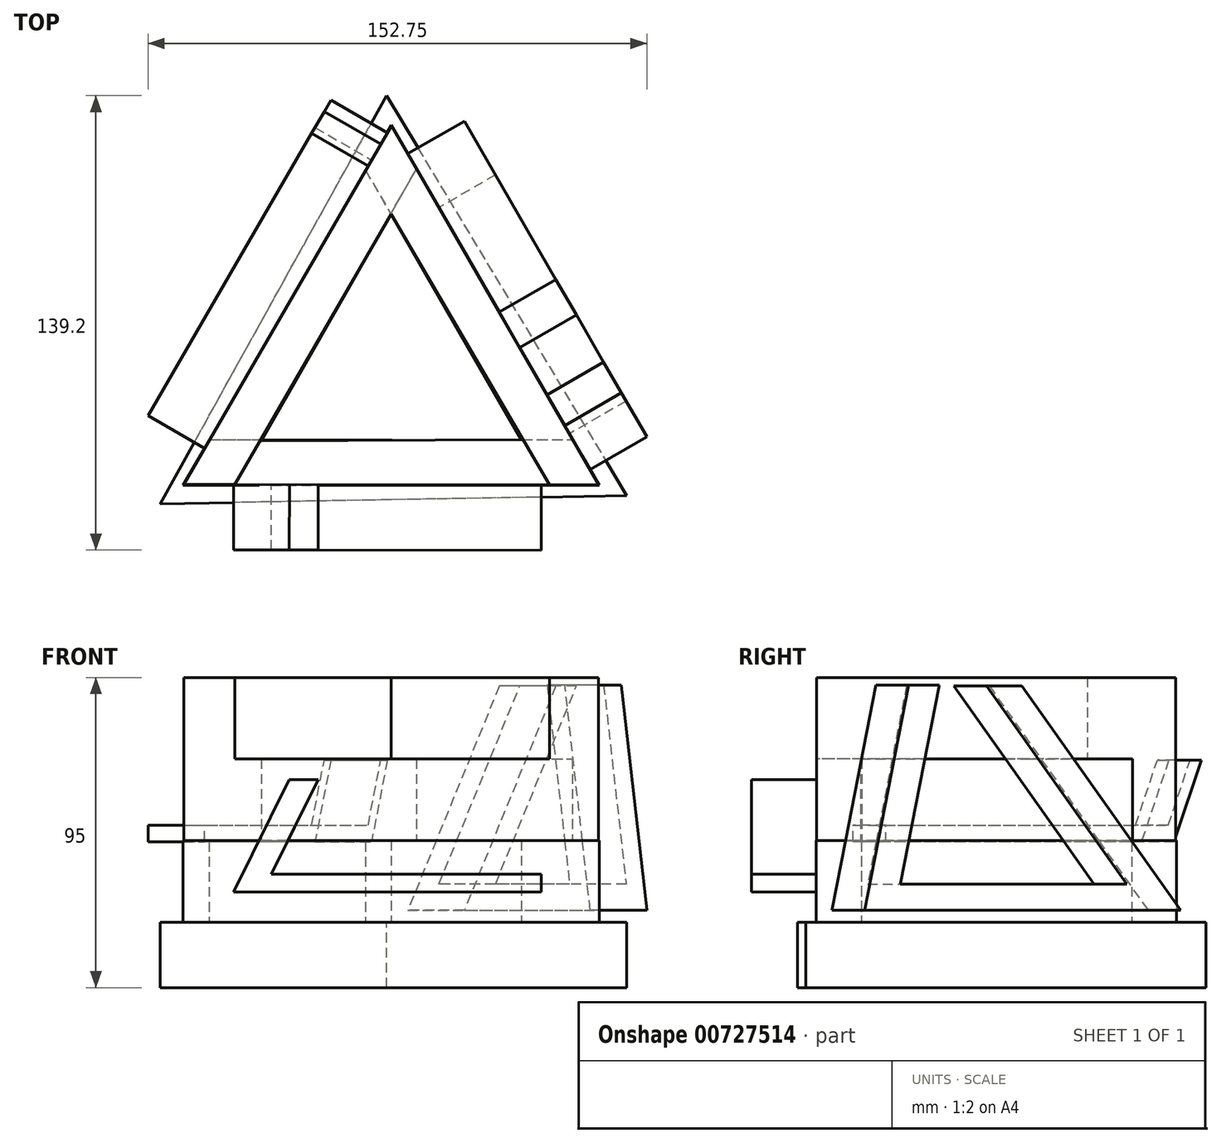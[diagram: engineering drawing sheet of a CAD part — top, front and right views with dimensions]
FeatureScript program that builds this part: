
annotation { "Feature Type Name" : "Feature", "Feature Type Description" : "" }
export const myFeature = defineFeature(function(context is Context, id is Id, definition is map)
    precondition{}
    {
        {
            var Q0;
            Q0=qCreatedBy(makeId("Top.planeOp"),FACE);
            var sketch = newSketch(context, id + "F0", { "sketchPlane" : qUnion([Q0])});
            skCircle(sketch, "E0.cCircle", {"center": v(0, 0) * mm, "radius": 41.26 * mm, "construction": true});
            skLineSegment(sketch, "E0.0", {"start": v(-1.43, 82.5) * mm, "end": v(72.16, -40) * mm});
            skLineSegment(sketch, "E0.1", {"start": v(72.16, -40) * mm, "end": v(-70.73, -42.5) * mm});
            skLineSegment(sketch, "E0.2", {"start": v(-70.73, -42.5) * mm, "end": v(-1.43, 82.5) * mm});
            skPoint(sketch, "E0.0.midPoint", {"position": v(35.37, 21.25) * mm});
            skSolve(sketch);
        }
        {
            var Q0;
            Q0=makeQuery(id+"F0.imprint","IMPRINT",FACE,{"disambiguationData":[TD([[makeQuery(id+"F0.imprint","IMPRINT",EDGE,{"derivedFrom":sQuery(id+"F0.wireOp",EDGE,"E0.0")}),-1.0]])]});
            var sketch = newSketch(context, id + "F1", { "sketchPlane" : qUnion([Q0])});
            skCircle(sketch, "E1.cCircle", {"center": v(0, 0) * mm, "radius": 36.78 * mm, "construction": true});
            skLineSegment(sketch, "E1.0", {"start": v(-63.71, -36.78) * mm, "end": v(0, 73.57) * mm, "construction": true});
            skLineSegment(sketch, "E1.1", {"start": v(0, 73.57) * mm, "end": v(63.71, -36.78) * mm});
            skLineSegment(sketch, "E1.2", {"start": v(63.71, -36.78) * mm, "end": v(-63.71, -36.78) * mm});
            skPoint(sketch, "E1.0.midPoint", {"position": v(-31.86, 18.4) * mm});
            skLineSegment(sketch, "E2", {"start": v(-31.86, 18.4) * mm, "end": v(63.71, -36.78) * mm, "construction": true});
            skLineSegment(sketch, "E3", {"start": v(-7.94, 59.81) * mm, "end": v(39.89, -23.03) * mm});
            skLineSegment(sketch, "E4", {"start": v(39.89, -23.03) * mm, "end": v(-55.77, -23.03) * mm});
            skLineSegment(sketch, "E5", {"start": v(-55.77, -23.03) * mm, "end": v(-63.71, -36.78) * mm});
            skLineSegment(sketch, "E6", {"start": v(0, 73.57) * mm, "end": v(-7.94, 59.81) * mm});
            skSolve(sketch);
        }
        {
            var Q0;
            Q0=makeQuery(id+"F0.imprint","IMPRINT",FACE,{"disambiguationData":[TD([[makeQuery(id+"F0.imprint","IMPRINT",EDGE,{"derivedFrom":sQuery(id+"F0.wireOp",EDGE,"E0.0")}),-1.0]])]});
            extrude(context, id + "F2", {"entities" : qUnion([Q0]), "oppositeDirection" : true, "depth" : 20 * mm, "offsetDistance" : 25 * mm});
        }
        {
            var Q0;
            Q0=makeQuery(id+"F1.imprint","IMPRINT",FACE,{"disambiguationData":[TD([[makeQuery(id+"F1.imprint","IMPRINT",EDGE,{"derivedFrom":sQuery(id+"F1.wireOp",EDGE,"E1.1")}),-1.0]])]});
            extrude(context, id + "F3", {"entities" : qUnion([Q0]), "operationType" : NewBodyOperationType.ADD, "depth" : 25 * mm, "offsetDistance" : 25 * mm});
        }
        {
            var Q0;
            Q0=qCreatedBy(makeId("Top.planeOp"),FACE);
            cPlane(context, id + "F4", {"entities" : qUnion([Q0]), "cplaneType" : CPlaneType.OFFSET, "offset" : 25 * mm, "width" : 150 * mm, "height" : 150 * mm});
        }
        {
            var Q0;
            Q0=qCreatedBy(id+"F4.planeOp",FACE);
            var sketch = newSketch(context, id + "F5", { "sketchPlane" : qUnion([Q0])});
            skCircle(sketch, "E7.cCircle", {"center": v(0, 0) * mm, "radius": 36.66 * mm, "construction": true});
            skLineSegment(sketch, "E7.1", {"start": v(63.45, -36.72) * mm, "end": v(-63.53, -36.6) * mm});
            skLineSegment(sketch, "E7.2", {"start": v(-63.53, -36.6) * mm, "end": v(0.07, 73.31) * mm});
            skPoint(sketch, "E7.0.midPoint", {"position": v(31.76, 18.3) * mm});
            skLineSegment(sketch, "E8", {"start": v(0.07, 73.31) * mm, "end": v(63.45, -36.72) * mm, "construction": true});
            skCircle(sketch, "E9.cCircle", {"center": v(0, 0) * mm, "radius": 23.03 * mm, "construction": true});
            skLineSegment(sketch, "E9.1", {"start": v(40, -22.83) * mm, "end": v(-39.77, -23.23) * mm});
            skLineSegment(sketch, "E9.2", {"start": v(-39.77, -23.23) * mm, "end": v(-0.23, 46.06) * mm});
            skPoint(sketch, "E9.0.midPoint", {"position": v(19.89, 11.62) * mm});
            skLineSegment(sketch, "E10", {"start": v(-0.23, 46.06) * mm, "end": v(7.73, 60.02) * mm});
            skLineSegment(sketch, "E11", {"start": v(7.73, 60.02) * mm, "end": v(0.07, 73.31) * mm});
            skLineSegment(sketch, "E12", {"start": v(40, -22.83) * mm, "end": v(55.45, -22.83) * mm});
            skLineSegment(sketch, "E13", {"start": v(55.45, -22.83) * mm, "end": v(63.45, -36.72) * mm});
            skSolve(sketch);
        }
        {
            var Q0;
            Q0=makeQuery(id+"F5.imprint","IMPRINT",FACE,{"disambiguationData":[TD([[makeQuery(id+"F5.imprint","IMPRINT",EDGE,{"derivedFrom":sQuery(id+"F5.wireOp",EDGE,"E7.1")}),-1.0]])]});
            extrude(context, id + "F6", {"entities" : qUnion([Q0]), "operationType" : NewBodyOperationType.ADD, "depth" : 25 * mm, "offsetDistance" : 25 * mm});
        }
        {
            var Q0;
            Q0=makeQuery(id+"F6.opExtrude","CAP_FACE",FACE,{"disambiguationData":[OSD([sQuery(id+"F5.wireOp",EDGE,"E7.1"),sQuery(id+"F5.wireOp",EDGE,"E7.2"),sQuery(id+"F5.wireOp",EDGE,"E9.1"),sQuery(id+"F5.wireOp",EDGE,"E9.2"),sQuery(id+"F5.wireOp",EDGE,"E10"),sQuery(id+"F5.wireOp",EDGE,"E11"),sQuery(id+"F5.wireOp",EDGE,"E12"),sQuery(id+"F5.wireOp",EDGE,"E13")])],"isStart":false});
            cPlane(context, id + "F7", {"entities" : qUnion([Q0]), "cplaneType" : CPlaneType.OFFSET, "offset" : 0 * mm, "width" : 150 * mm, "height" : 150 * mm});
        }
        {
            var Q0;
            Q0=qCreatedBy(id+"F7.planeOp",FACE);
            var sketch = newSketch(context, id + "F8", { "sketchPlane" : qUnion([Q0])});
            skCircle(sketch, "E14.cCircle", {"center": v(0, 0) * mm, "radius": 36.66 * mm, "construction": true});
            skLineSegment(sketch, "E14.1", {"start": v(63.45, -36.72) * mm, "end": v(-63.53, -36.6) * mm, "construction": true});
            skLineSegment(sketch, "E14.2", {"start": v(-63.53, -36.6) * mm, "end": v(0.07, 73.31) * mm});
            skPoint(sketch, "E14.0.midPoint", {"position": v(31.75, 18.31) * mm});
            skPoint(sketch, "E15.0.midPoint", {"position": v(20.21, 11.87) * mm});
            skLineSegment(sketch, "E16", {"start": v(0.07, 73.31) * mm, "end": v(63.45, -36.72) * mm});
            skLineSegment(sketch, "E17", {"start": v(0, 46.22) * mm, "end": v(-47.93, -36.6) * mm});
            skLineSegment(sketch, "E18", {"start": v(-47.93, -36.6) * mm, "end": v(-63.53, -36.6) * mm});
            skLineSegment(sketch, "E19", {"start": v(0, 46.22) * mm, "end": v(48.44, -36.7) * mm});
            skLineSegment(sketch, "E20", {"start": v(48.44, -36.7) * mm, "end": v(63.45, -36.72) * mm});
            skSolve(sketch);
        }
        {
            var Q0;
            Q0=makeQuery(id+"F8.imprint","IMPRINT",FACE,{"disambiguationData":[TD([[makeQuery(id+"F8.imprint","IMPRINT",EDGE,{"derivedFrom":sQuery(id+"F8.wireOp",EDGE,"E14.2")}),-1.0]])]});
            extrude(context, id + "F9", {"entities" : qUnion([Q0]), "operationType" : NewBodyOperationType.ADD, "depth" : 25 * mm, "offsetDistance" : 25 * mm});
        }
        {
            var Q0;
            Q0=makeQuery(id+"F6.opExtrude","SWEPT_FACE",FACE,{"disambiguationData":[OSD([sQuery(id+"F5.wireOp",EDGE,"E7.1")])]});
            cPlane(context, id + "F10", {"entities" : qUnion([Q0]), "cplaneType" : CPlaneType.OFFSET, "offset" : 0 * mm, "width" : 150 * mm, "height" : 150 * mm});
        }
        {
            var Q0;
            Q0=qCreatedBy(id+"F10.planeOp",FACE);
            var sketch = newSketch(context, id + "F11", { "sketchPlane" : qUnion([Q0])});
            skLineSegment(sketch, "E21", {"start": v(-48.22, 9.28) * mm, "end": v(45.96, 9.28) * mm});
            skLineSegment(sketch, "E22", {"start": v(45.96, 9.28) * mm, "end": v(45.96, 14.78) * mm});
            skLineSegment(sketch, "E23", {"start": v(45.96, 14.78) * mm, "end": v(-36.64, 14.78) * mm});
            skLineSegment(sketch, "E24", {"start": v(-36.64, 14.78) * mm, "end": v(-22.3, 43.74) * mm});
            skLineSegment(sketch, "E25", {"start": v(-22.3, 43.74) * mm, "end": v(-31.15, 43.74) * mm});
            skLineSegment(sketch, "E26", {"start": v(-31.15, 43.74) * mm, "end": v(-48.22, 9.28) * mm});
            skSolve(sketch);
        }
        {
            var Q0;
            Q0=makeQuery(id+"F11.imprint","IMPRINT",FACE,{"disambiguationData":[TD([[makeQuery(id+"F11.imprint","IMPRINT",EDGE,{"derivedFrom":sQuery(id+"F11.wireOp",EDGE,"E21")}),1.0]])]});
            extrude(context, id + "F12", {"entities" : qUnion([Q0]), "operationType" : NewBodyOperationType.ADD, "depth" : 20 * mm, "offsetDistance" : 25 * mm});
        }
        {
            var Q0;
            Q0=makeQuery(id+"F6.opExtrude","SWEPT_FACE",FACE,{"disambiguationData":[OSD([sQuery(id+"F5.wireOp",EDGE,"E7.2")])]});
            cPlane(context, id + "F13", {"entities" : qUnion([Q0]), "cplaneType" : CPlaneType.OFFSET, "offset" : 0 * mm, "width" : 150 * mm, "height" : 150 * mm});
        }
        {
            var Q0;
            Q0=qCreatedBy(id+"F13.planeOp",FACE);
            var sketch = newSketch(context, id + "F14", { "sketchPlane" : qUnion([Q0])});
            skLineSegment(sketch, "E27", {"start": v(-49.25, 24.63) * mm, "end": v(50.75, 24.63) * mm});
            skLineSegment(sketch, "E28", {"start": v(50.75, 24.63) * mm, "end": v(50.75, 29.76) * mm});
            skLineSegment(sketch, "E29", {"start": v(50.75, 29.76) * mm, "end": v(-49.25, 29.76) * mm});
            skLineSegment(sketch, "E30", {"start": v(-49.25, 29.76) * mm, "end": v(-56.94, 49.66) * mm});
            skLineSegment(sketch, "E31", {"start": v(-56.94, 49.66) * mm, "end": v(-60.99, 49.66) * mm});
            skLineSegment(sketch, "E32", {"start": v(-60.99, 49.66) * mm, "end": v(-51.32, 24.63) * mm});
            skLineSegment(sketch, "E33", {"start": v(-51.32, 24.63) * mm, "end": v(-43.6, 24.63) * mm});
            skSolve(sketch);
        }
        {
            var Q0;
            {var subQ0=sQuery(id+"F14.wireOp",EDGE,"E27");Q0=makeQuery(id+"F14.imprint","IMPRINT",FACE,{"disambiguationData":[TD([[makeQuery(id+"F14.imprint","IMPRINT",EDGE,{"derivedFrom":subQ0}),1.0]])]});}
            extrude(context, id + "F15", {"entities" : qUnion([Q0]), "operationType" : NewBodyOperationType.ADD, "depth" : 20 * mm, "offsetDistance" : 25 * mm});
        }
        {
            var Q0;
            Q0=makeQuery(id+"F3.opExtrude","SWEPT_FACE",FACE,{"disambiguationData":[OSD([sQuery(id+"F1.wireOp",EDGE,"E1.1")])]});
            cPlane(context, id + "F16", {"entities" : qUnion([Q0]), "cplaneType" : CPlaneType.OFFSET, "offset" : 0 * mm, "width" : 150 * mm, "height" : 150 * mm});
        }
        {
            var Q0;
            Q0=qCreatedBy(id+"F16.planeOp",FACE);
            var sketch = newSketch(context, id + "F17", { "sketchPlane" : qUnion([Q0])});
            skLineSegment(sketch, "E34", {"start": v(-42.65, 72.72) * mm, "end": v(-31.77, 72.72) * mm});
            skLineSegment(sketch, "E35", {"start": v(-31.77, 72.72) * mm, "end": v(-45.54, 11.71) * mm});
            skLineSegment(sketch, "E36", {"start": v(-45.54, 11.71) * mm, "end": v(34.46, 11.71) * mm});
            skLineSegment(sketch, "E37", {"start": v(34.46, 11.71) * mm, "end": v(-15.06, 72.4) * mm});
            skLineSegment(sketch, "E38", {"start": v(-15.06, 72.4) * mm, "end": v(-2.53, 72.4) * mm});
            skLineSegment(sketch, "E39", {"start": v(-2.53, 72.4) * mm, "end": v(53.52, 3.72) * mm});
            skLineSegment(sketch, "E40", {"start": v(53.52, 3.72) * mm, "end": v(-58.22, 3.72) * mm});
            skLineSegment(sketch, "E41", {"start": v(-58.22, 3.72) * mm, "end": v(-42.65, 72.72) * mm});
            skSolve(sketch);
        }
        {
            var Q0;
            Q0=makeQuery(id+"F17.imprint","IMPRINT",FACE,{"disambiguationData":[TD([[makeQuery(id+"F17.imprint","IMPRINT",EDGE,{"derivedFrom":sQuery(id+"F17.wireOp",EDGE,"E34")}),-1.0]])]});
            extrude(context, id + "F18", {"entities" : qUnion([Q0]), "operationType" : NewBodyOperationType.ADD, "depth" : 20 * mm, "offsetDistance" : 25 * mm});
        }
    });
